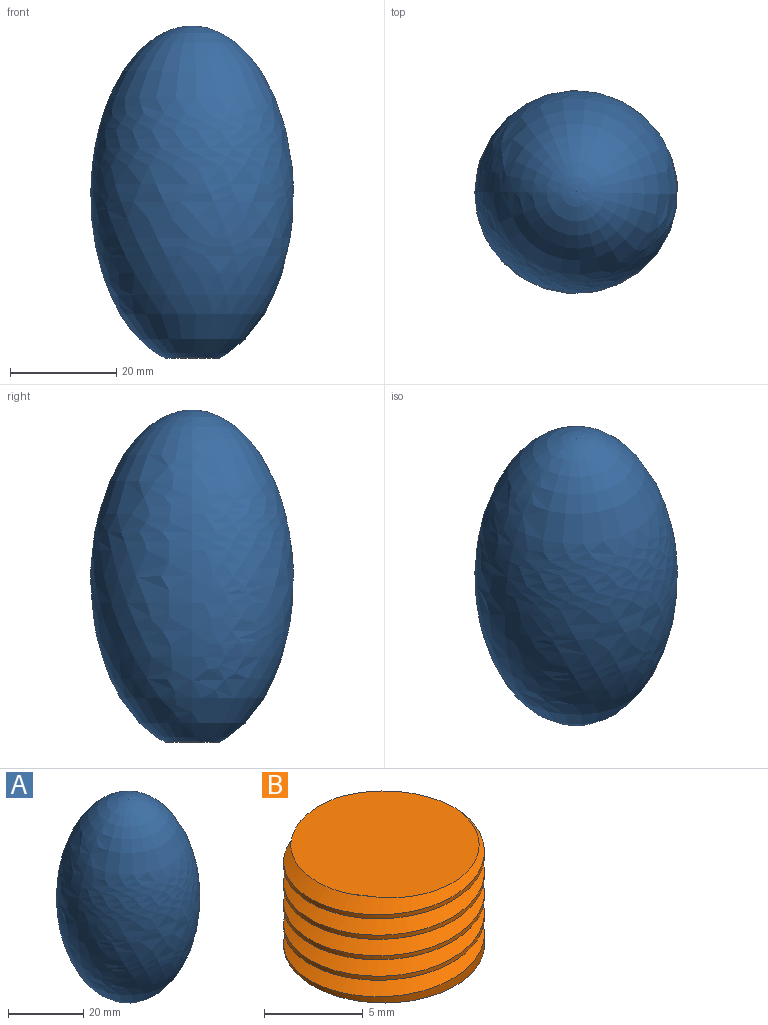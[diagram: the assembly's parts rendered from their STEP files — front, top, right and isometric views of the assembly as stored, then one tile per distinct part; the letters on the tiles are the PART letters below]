
ASSEMBLY  parts=2 mates=1
PART A: 8 faces, bbox 38.1x38.1x62.5 mm
  f0: revolved ~62.35x38.06mm, area 6600mm2, adj f1
  f1: cylinder r=5.08mm len=10.16mm, axis (0,0,-1), area 50.1mm2, adj f0,f2,f5,f6,f7
  f2: revolved ~51.32x27.93mm, area 3887.8mm2, adj f1,f3
  f3: cylinder r=5.08mm len=10.16mm, axis (0,0,-1), area 12.9mm2, adj f2,f4,f7
  f4: plane 1.02x0.88mm, normal (0,1,0), area 0.4mm2, adj f3,f6,f7
  f5: plane 1.02x0.81mm, normal (0.92,0.39,0), area 0.4mm2, adj f1,f6,f7
  f6: bspline ~11.73x10.16mm, area 139mm2, adj f1,f4,f5,f7
  f7: bspline ~11.73x10.16mm, area 139mm2, adj f1,f3,f4,f5,f6
PART B: 6 faces, bbox 10.7x12.3x7.3 mm
  f0: revolved ~9.76x7.06mm, area 0mm2, adj f1
  f1: cylinder r=5.08mm len=10.16mm, axis (0,0,-1), area 50.1mm2, adj f0,f2,f3,f4,f5
  f2: plane 10.1x10.08mm, normal (0,0,1), area 70.5mm2, adj f1,f3,f5
  f3: bspline ~11.73x10.16mm, area 133.3mm2, adj f1,f2,f4,f5
  f4: plane 1.02x0.81mm, normal (-0.92,-0.39,0), area 0.4mm2, adj f1,f3,f5
  f5: bspline ~11.73x10.16mm, area 120.9mm2, adj f1,f2,f3,f4
PLACE A t=(-1.54,-8.38,-28.1)mm
PLACE B t=(-1.54,-8.38,-25.23)mm
MATE cylindrical A.f1 <-> B.f1  axis (0,0,-1) through (-1.54,-8.38,-58.7)mm
